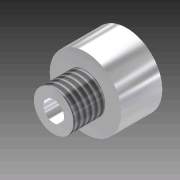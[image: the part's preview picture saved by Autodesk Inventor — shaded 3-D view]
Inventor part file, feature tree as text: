
AUTODESK INVENTOR PART (.ipt)
format: ipt  version: 2011 (Build 150239000, 239)  size: 119,808 bytes
history: native  units: in
note: dims shown in document units (in); Inventor stores cm internally (conversion verified against a paired STEP export)
features: extrude x5, sketch x5, thread x1, plane x1, projected_geometry x1
ambient origin geometry x8: Origin, YZ Plane, XZ Plane, XY Plane, X Axis, Y Axis, Z Axis, Center Point
bodies: Solid1 (feature_tree)
feature tree (13):
  extrude  "Extrusion1"  Depth=0.95in
  extrude  "Extrusion2"  Depth=0.1in TaperAngle=0.0deg
  extrude  "Extrusion3"  Depth=0.5in TaperAngle=0.0deg
  thread  "Thread1"  [1 undecoded]
  plane  "Work Plane1"
  extrude  "Extrusion4"  Depth=0.425in
  extrude  "Extrusion5"  Depth=0.5in TaperAngle=0.0deg
  sketch  "Sketch1"  dims[d0=1.125in d1=0.95in]
  sketch  "Sketch2"  dims[d2=0.55in d3=0.0in d4=0.1in d5=0.0in]
  sketch  "Sketch3"  dims[d6=0.625in d7=0.5in d8=0.0in d9=1.0in d10=0.0in]
  sketch  "Sketch4"  dims[d11=-0.5625in d12=0.425in]
  projected_geometry  "Projected Loop1"
  sketch  "Sketch5"  dims[d13=0.325in d14=0.5in d15=0.0in d16=0.325in d17=0.5in d18=0.0in]
note: 1 required parameter value undecoded (feature->parameter linkage not recoverable at this tier; creation-order binding heuristic only, values carry confidence <= 0.55)
